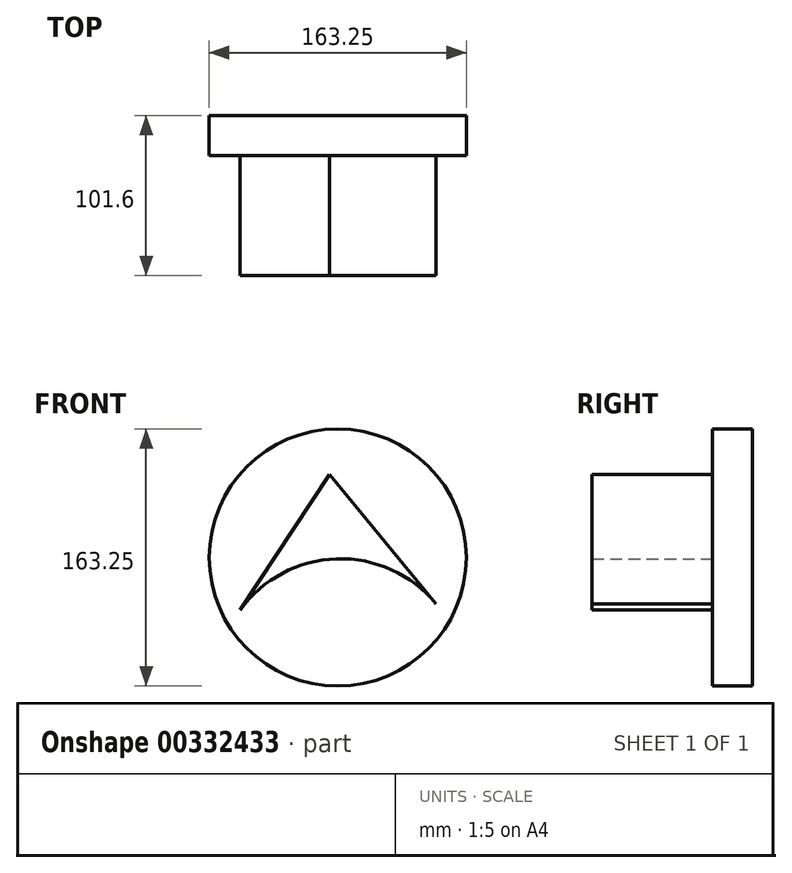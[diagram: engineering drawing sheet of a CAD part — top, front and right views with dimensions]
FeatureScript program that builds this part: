
annotation { "Feature Type Name" : "Feature", "Feature Type Description" : "" }
export const myFeature = defineFeature(function(context is Context, id is Id, definition is map)
    precondition{}
    {
        {
            var Q0;
            Q0=qCreatedBy(makeId("Front.planeOp"),FACE);
            var sketch = newSketch(context, id + "F0", { "sketchPlane" : qUnion([Q0])});
            skCircle(sketch, "E0", {"center": v(-32.55, 13.37) * mm, "radius": 81.62 * mm});
            skSolve(sketch);
        }
        {
            var Q0;
            Q0 = qSketchRegion(id + "F0", true);
            extrude(context, id + "F1", {"entities" : qUnion([Q0]), "depth" : 25.4 * mm});
        }
        {
            var Q0;
            Q0=makeQuery(id+"F1.opExtrude","CAP_FACE",FACE,{"disambiguationData":[OSD([sQuery(id+"F0.wireOp",EDGE,"E0")])],"isStart":false});
            var sketch = newSketch(context, id + "F2", { "sketchPlane" : qUnion([Q0])});
            skLineSegment(sketch, "E1", {"start": v(-94.51, -20.02) * mm, "end": v(-37.9, 66.02) * mm});
            skLineSegment(sketch, "E2", {"start": v(-37.9, 66.02) * mm, "end": v(29.87, -16) * mm});
            skArc(sketch, "E3", {"start": v(29.87, -16) * mm, "mid": v(-33.3, 12.51) * mm, "end": v(-94.51, -20.02) * mm});
            skSolve(sketch);
        }
        {
            var Q0;
            Q0=makeQuery(id+"F2.imprint","IMPRINT",FACE,{"disambiguationData":[TD([[makeQuery(id+"F2.imprint","IMPRINT",EDGE,{"derivedFrom":sQuery(id+"F2.wireOp",EDGE,"E1")}),-1.0]])]});
            extrude(context, id + "F3", {"entities" : qUnion([Q0]), "operationType" : NewBodyOperationType.ADD, "depth" : 76.2 * mm});
        }
    });
